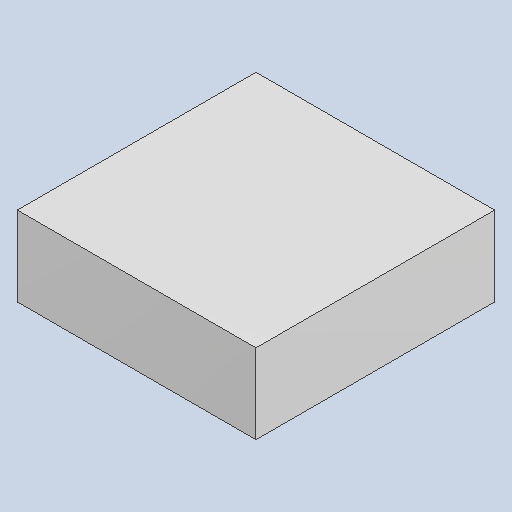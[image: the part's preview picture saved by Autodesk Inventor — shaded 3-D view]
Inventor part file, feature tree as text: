
AUTODESK INVENTOR PART (.ipt)
format: ipt  version: 2023.4 (Build 274418000, 418)  size: 79,872 bytes
history: native  units: mm
features: extrude x1
ambient origin geometry x8: Origin, YZ Plane, XZ Plane, XY Plane, X Axis, Y Axis, Z Axis, Center Point
bodies: Solid1 (feature_tree)
feature tree (1):
  extrude  "Extruded_14"  [1 undecoded]
note: 1 required parameter value undecoded (feature->parameter linkage not recoverable at this tier; creation-order binding heuristic only, values carry confidence <= 0.55)
